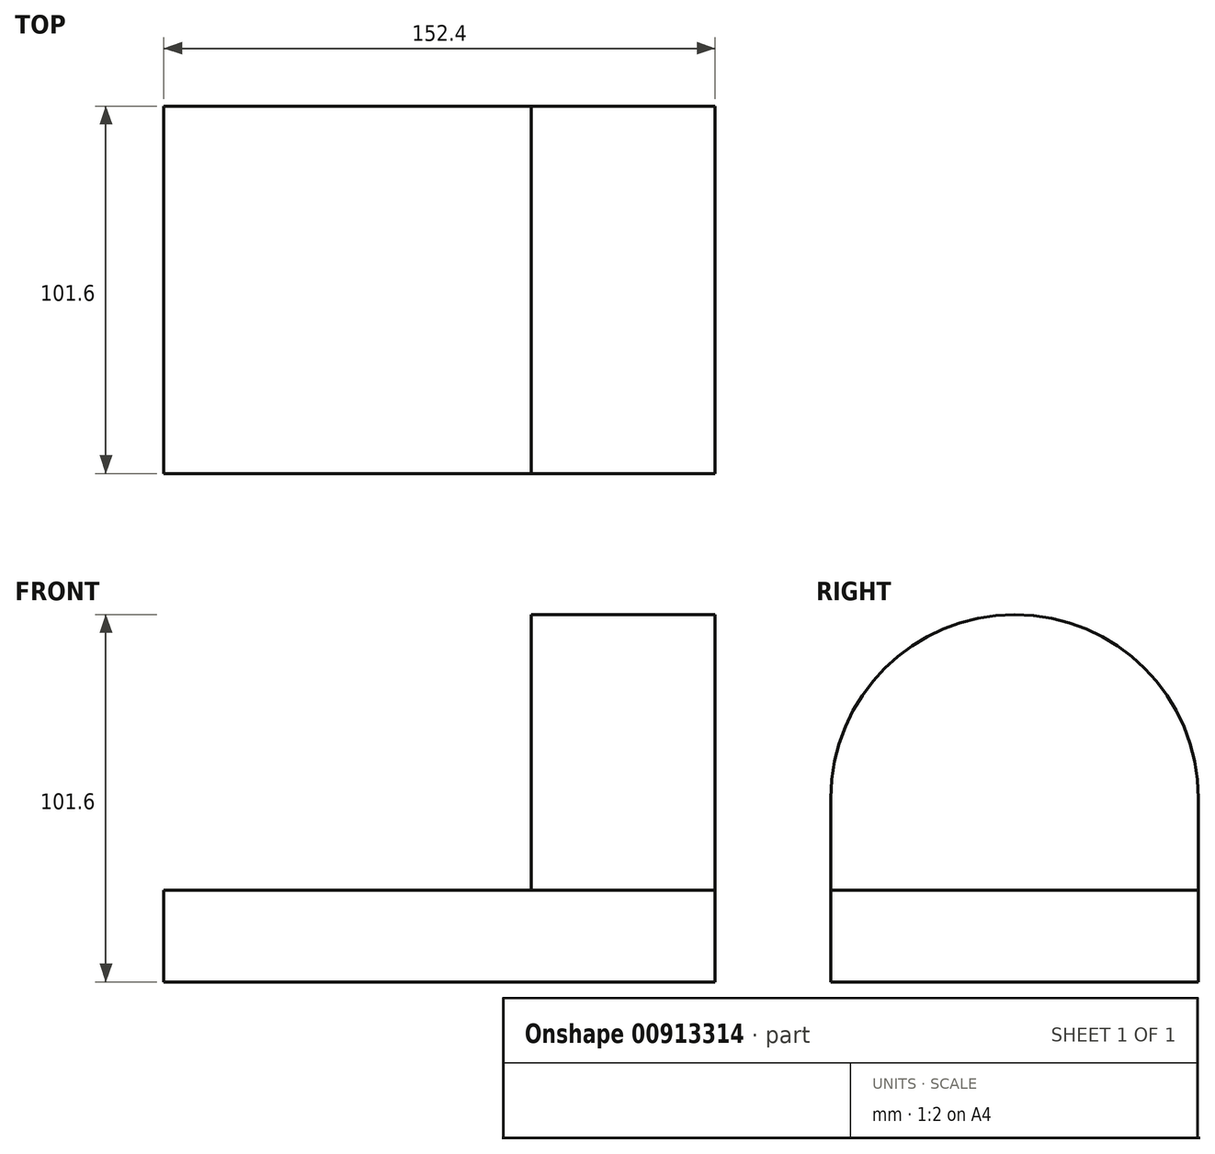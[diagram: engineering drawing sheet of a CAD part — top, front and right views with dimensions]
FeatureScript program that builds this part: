
annotation { "Feature Type Name" : "Feature", "Feature Type Description" : "" }
export const myFeature = defineFeature(function(context is Context, id is Id, definition is map)
    precondition{}
    {
        {
            var Q0;
            Q0=qCreatedBy(makeId("Top.planeOp"),FACE);
            var sketch = newSketch(context, id + "F0", { "sketchPlane" : qUnion([Q0])});
            skLineSegment(sketch, "E0.bottom", {"start": v(0, 0) * mm, "end": v(152.4, 0) * mm});
            skLineSegment(sketch, "E0.top", {"start": v(0, -101.6) * mm, "end": v(152.4, -101.6) * mm});
            skLineSegment(sketch, "E0.left", {"start": v(0, 0) * mm, "end": v(0, -101.6) * mm});
            skLineSegment(sketch, "E0.right", {"start": v(152.4, 0) * mm, "end": v(152.4, -101.6) * mm});
            skSolve(sketch);
        }
        {
            var Q0;
            Q0 = qSketchRegion(id + "F0", true);
            extrude(context, id + "F1", {"entities" : qUnion([Q0]), "depth" : 25.4 * mm, "offsetDistance" : 25.4 * mm});
        }
        {
            var Q0;
            Q0=makeQuery(id+"F1.opExtrude","SWEPT_FACE",FACE,{"disambiguationData":[OSD([sQuery(id+"F0.wireOp",EDGE,"E0.right")])]});
            var sketch = newSketch(context, id + "F2", { "sketchPlane" : qUnion([Q0])});
            skLineSegment(sketch, "E1.bottom", {"start": v(-101.6, 25.4) * mm, "end": v(0, 25.4) * mm});
            skLineSegment(sketch, "E1.top", {"start": v(-101.6, 50.8) * mm, "end": v(0, 50.8) * mm});
            skLineSegment(sketch, "E1.left", {"start": v(-101.6, 25.4) * mm, "end": v(-101.6, 50.8) * mm});
            skLineSegment(sketch, "E1.right", {"start": v(0, 25.4) * mm, "end": v(0, 50.8) * mm});
            skArc(sketch, "E2", {"start": v(0, 50.8) * mm, "mid": v(-50.8, 101.6) * mm, "end": v(-101.6, 50.8) * mm});
            skSolve(sketch);
        }
        {
            var Q0;
            Q0 = qSketchRegion(id + "F2", true);
            extrude(context, id + "F3", {"entities" : qUnion([Q0]), "oppositeDirection" : true, "depth" : 50.8 * mm, "offsetDistance" : 25.4 * mm});
        }
    });
